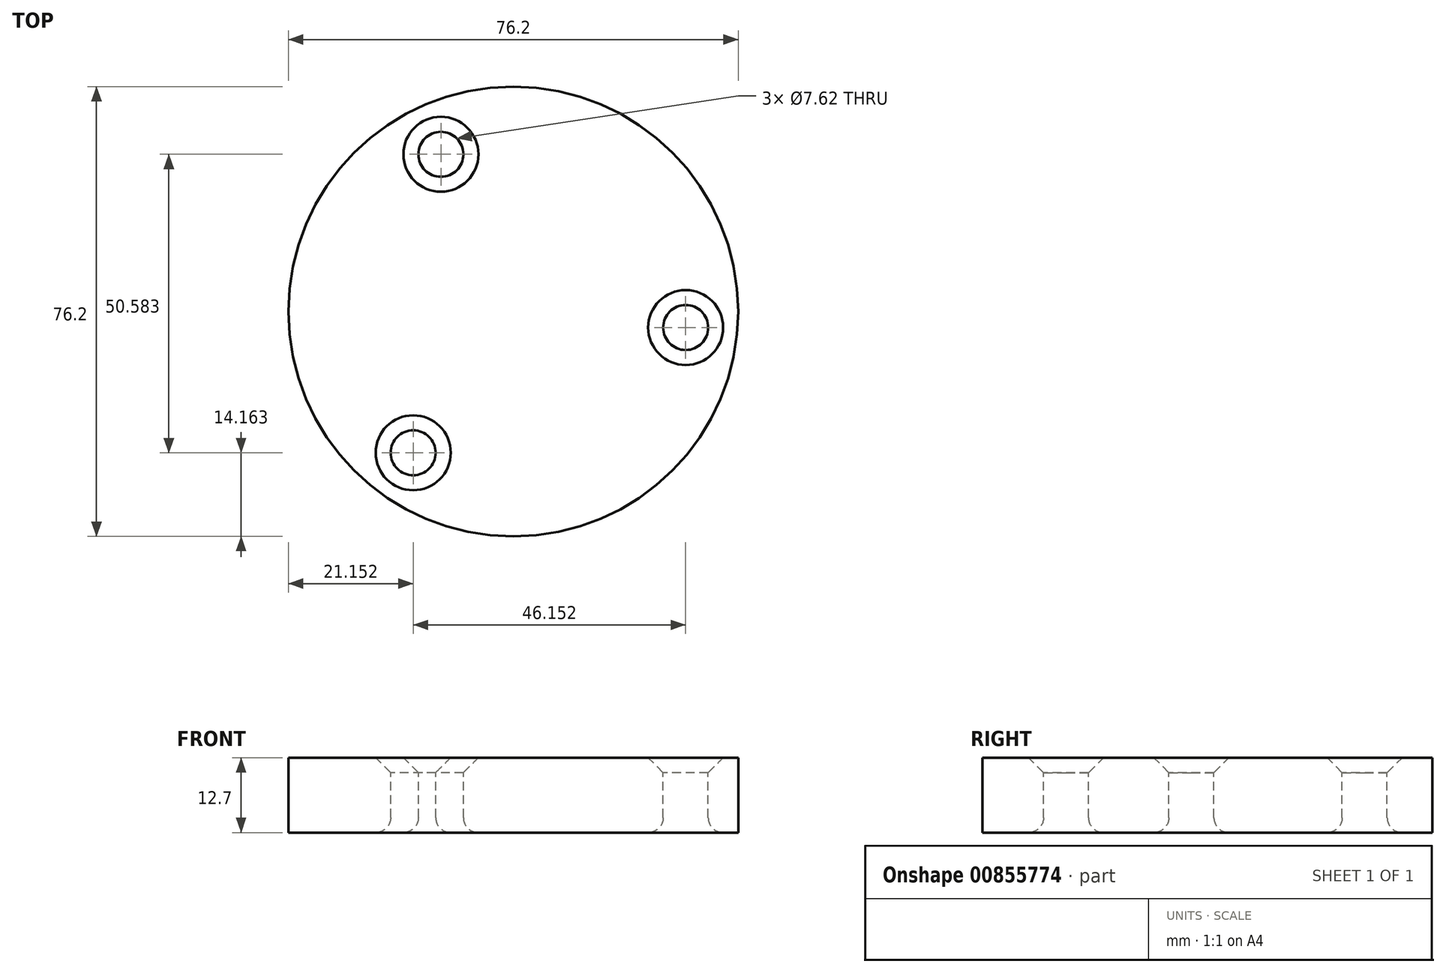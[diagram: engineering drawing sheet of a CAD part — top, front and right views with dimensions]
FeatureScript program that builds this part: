
annotation { "Feature Type Name" : "Feature", "Feature Type Description" : "" }
export const myFeature = defineFeature(function(context is Context, id is Id, definition is map)
    precondition{}
    {
        {
            var Q0;
            Q0=qCreatedBy(makeId("Top.planeOp"),FACE);
            var sketch = newSketch(context, id + "F0", { "sketchPlane" : qUnion([Q0])});
            skCircle(sketch, "E0", {"center": v(0, 0) * mm, "radius": 38.1 * mm});
            skPoint(sketch, "E1.0.midPoint", {"position": v(8.47, 11.97) * mm});
            skCircle(sketch, "E2", {"center": v(-12.26, 26.65) * mm, "radius": 6.35 * mm});
            skCircle(sketch, "E3", {"center": v(-16.95, -23.94) * mm, "radius": 6.35 * mm});
            skCircle(sketch, "E4", {"center": v(29.2, -2.7) * mm, "radius": 6.35 * mm});
            skSolve(sketch);
        }
        {
            var Q0;
            Q0=makeQuery(id+"F0.imprint","IMPRINT",FACE,{"disambiguationData":[TD([[makeQuery(id+"F0.imprint","IMPRINT",EDGE,{"derivedFrom":sQuery(id+"F0.wireOp",EDGE,"E0")}),1.0]])]});
            extrude(context, id + "F1", {"entities" : qUnion([Q0]), "depth" : 12.7 * mm, "offsetDistance" : 25.4 * mm});
        }
        {
            var Q0;
            Q0=makeQuery(id+"F1.opExtrude","CAP_FACE",FACE,{"disambiguationData":[OSD([sQuery(id+"F0.wireOp",EDGE,"E0"),sQuery(id+"F0.wireOp",EDGE,"E2"),sQuery(id+"F0.wireOp",EDGE,"E3"),sQuery(id+"F0.wireOp",EDGE,"E4")])],"isStart":false});
            var sketch = newSketch(context, id + "F2", { "sketchPlane" : qUnion([Q0])});
            skCircle(sketch, "E5.0", {"center": v(-12.26, 26.65) * mm, "radius": 3.81 * mm});
            skCircle(sketch, "E6.0", {"center": v(-16.95, -23.94) * mm, "radius": 3.81 * mm});
            skCircle(sketch, "E7.0", {"center": v(29.2, -2.7) * mm, "radius": 3.81 * mm});
            skSolve(sketch);
        }
        {
            var Q0;
            Q0=makeQuery(id+"F2.imprint","IMPRINT",FACE,{"disambiguationData":[TD([[makeQuery(id+"F2.imprint","IMPRINT",EDGE,{"derivedFrom":sQuery(id+"F2.wireOp",EDGE,"E6.0")}),-1.0]])]});
            var Q1;
            Q1=makeQuery(id+"F2.imprint","IMPRINT",FACE,{"disambiguationData":[TD([[makeQuery(id+"F2.imprint","IMPRINT",EDGE,{"derivedFrom":sQuery(id+"F2.wireOp",EDGE,"E5.0")}),-1.0]])]});
            var Q2;
            Q2=makeQuery(id+"F2.imprint","IMPRINT",FACE,{"disambiguationData":[TD([[makeQuery(id+"F2.imprint","IMPRINT",EDGE,{"derivedFrom":sQuery(id+"F2.wireOp",EDGE,"E7.0")}),-1.0]])]});
            extrude(context, id + "F3", {"entities" : qUnion([Q0, Q1, Q2]), "operationType" : NewBodyOperationType.ADD, "oppositeDirection" : true, "depth" : 12.7 * mm, "offsetDistance" : 25.4 * mm});
        }
        {
            var Q0;
            Q0=makeQuery(id+"F3.opExtrude","CAP_EDGE",EDGE,{"disambiguationData":[OSD([sQuery(id+"F2.wireOp",EDGE,"E7.0")])],"isStart":false});
            var Q1;
            Q1=makeQuery(id+"F3.opExtrude","CAP_EDGE",EDGE,{"disambiguationData":[OSD([sQuery(id+"F2.wireOp",EDGE,"E5.0")])],"isStart":false});
            var Q2;
            Q2=makeQuery(id+"F3.opExtrude","CAP_EDGE",EDGE,{"disambiguationData":[OSD([sQuery(id+"F2.wireOp",EDGE,"E6.0")])],"isStart":false});
            fillet(context, id + "F4", {"entities" : qUnion([Q0, Q1, Q2]), "radius" : 2.54 * mm, "tangentPropagation" : true, "allowEdgeOverflow" : false});
        }
        {
            var Q0;
            Q0=makeQuery(id+"F3.opExtrude","CAP_EDGE",EDGE,{"disambiguationData":[OSD([sQuery(id+"F2.wireOp",EDGE,"E5.0")])],"isStart":true});
            var Q1;
            Q1=makeQuery(id+"F3.opExtrude","CAP_EDGE",EDGE,{"disambiguationData":[OSD([sQuery(id+"F2.wireOp",EDGE,"E7.0")])],"isStart":true});
            var Q2;
            Q2=makeQuery(id+"F3.opExtrude","CAP_EDGE",EDGE,{"disambiguationData":[OSD([sQuery(id+"F2.wireOp",EDGE,"E6.0")])],"isStart":true});
            chamfer(context, id + "F5", {"entities" : qUnion([Q0, Q1, Q2]), "width" : 2.54 * mm, "tangentPropagation" : true});
        }
    });
